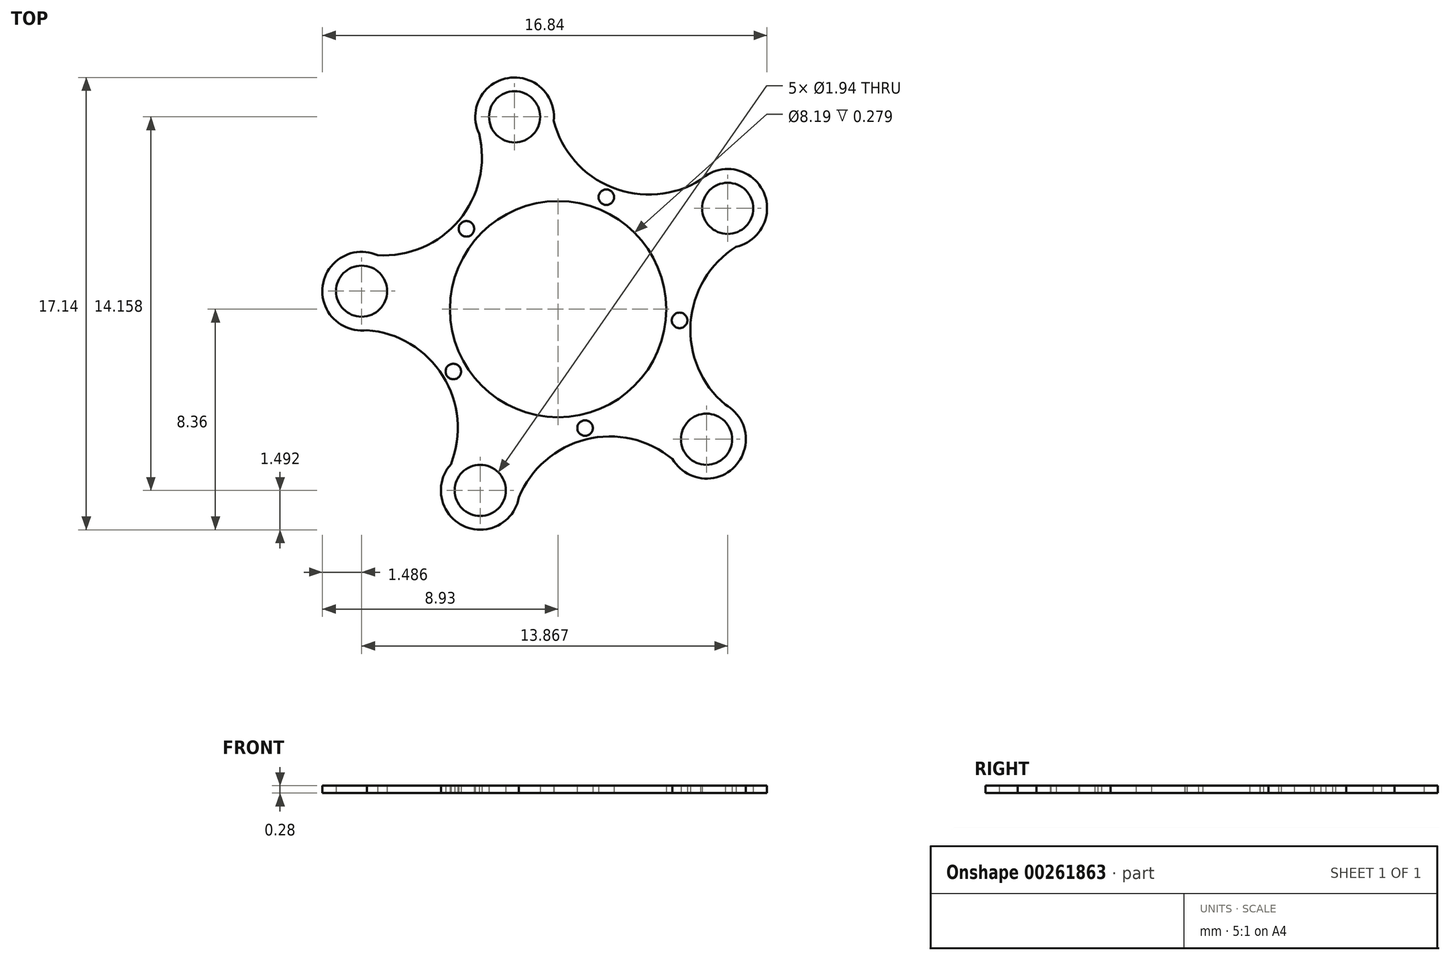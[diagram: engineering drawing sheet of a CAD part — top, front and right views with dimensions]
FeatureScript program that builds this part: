
annotation { "Feature Type Name" : "Feature", "Feature Type Description" : "" }
export const myFeature = defineFeature(function(context is Context, id is Id, definition is map)
    precondition{}
    {
        {
            var Q0;
            Q0=qCreatedBy(makeId("Top.planeOp"),FACE);
            var sketch = newSketch(context, id + "F0", { "sketchPlane" : qUnion([Q0])});
            skCircle(sketch, "E0", {"center": v(5.62, -4.93) * mm, "radius": 0.97 * mm});
            skCircle(sketch, "E1", {"center": v(6.42, 3.82) * mm, "radius": 0.97 * mm});
            skCircle(sketch, "E2", {"center": v(-2.95, -6.87) * mm, "radius": 0.97 * mm});
            skCircle(sketch, "E3", {"center": v(-7.44, 0.68) * mm, "radius": 0.97 * mm});
            skCircle(sketch, "E4", {"center": v(-1.65, 7.3) * mm, "radius": 0.97 * mm});
            skCircle(sketch, "E5", {"center": v(5.62, -4.93) * mm, "radius": 1.5 * mm});
            skCircle(sketch, "E6", {"center": v(6.42, 3.82) * mm, "radius": 1.5 * mm});
            skCircle(sketch, "E7", {"center": v(-1.65, 7.3) * mm, "radius": 1.5 * mm});
            skCircle(sketch, "E8", {"center": v(-7.44, 0.68) * mm, "radius": 1.5 * mm});
            skArc(sketch, "E9", {"start": v(-4.06, -5.87) * mm, "mid": v(-4.37, -2.53) * mm, "end": v(-7.25, -0.8) * mm});
            skArc(sketch, "E10", {"start": v(-6.84, 2.05) * mm, "mid": v(-3.75, 3.37) * mm, "end": v(-3, 6.65) * mm});
            skArc(sketch, "E11", {"start": v(-0.17, 7.14) * mm, "mid": v(2.05, 4.61) * mm, "end": v(5.4, 4.9) * mm});
            skArc(sketch, "E12", {"start": v(6.74, 2.36) * mm, "mid": v(5.02, -0.52) * mm, "end": v(6.33, -3.62) * mm});
            skCircle(sketch, "E13", {"center": v(-2.95, -6.87) * mm, "radius": 1.5 * mm});
            skArc(sketch, "E14", {"start": v(4.33, -5.68) * mm, "mid": v(1.05, -4.93) * mm, "end": v(-1.48, -7.14) * mm});
            skCircle(sketch, "E15", {"center": v(-3.47, 3.05) * mm, "radius": 0.3 * mm});
            skCircle(sketch, "E16", {"center": v(1.82, 4.24) * mm, "radius": 0.3 * mm});
            skCircle(sketch, "E17", {"center": v(4.6, -0.42) * mm, "radius": 0.3 * mm});
            skCircle(sketch, "E18", {"center": v(1.02, -4.5) * mm, "radius": 0.3 * mm});
            skCircle(sketch, "E19", {"center": v(-3.97, -2.36) * mm, "radius": 0.3 * mm});
            skCircle(sketch, "E20", {"center": v(0, 0) * mm, "radius": 4.1 * mm});
            skSolve(sketch);
        }
        {
            var Q0;
            Q0 = qSketchRegion(id + "F0", true);
            extrude(context, id + "F1", {"entities" : qUnion([Q0]), "depth" : 0.28 * mm});
        }
    });
